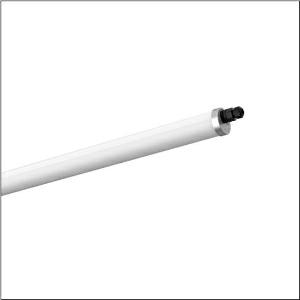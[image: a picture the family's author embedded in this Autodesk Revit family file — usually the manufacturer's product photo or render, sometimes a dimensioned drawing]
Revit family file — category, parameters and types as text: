
# Revit family: monsun_r__31_tube_51ft107n4a0a_c9dd
name_source: partatom
category: Lighting Fixtures
units: mm (PartAtom-declared; Revit-internal decimal feet)

## family parameters
Cut with Voids When Loaded = No
Host = Face
Light Source = No
Part Type = Normal
Room Calculation Point = No
Round Connector Dimension = Use Diameter
Shared = No

## types (1)
- Monsun® 31 Tube (1 x LED, 10000 lm, 58 W, 4000K)
    Apparent Load = 58 VA
    CIE Flux Codes = 42 71 90 91 100
    Color Rendering = 80
    Color Temperature = 4000K
    Default Elevation = 1800 mm
    Description = Monsun® 31 Tube, tubular luminaire, primary optical cover: diffuser, of PMMA, light emission: direct distribution, primary light characteristic: symmetric, installation type: suspended mounting, surface-mounted, LED, rated luminous flux: 10.000lm, luminous efficacy: 160lm/W, light colour: 840, colour temperature: 4000K, with with 1 terminal, 3-pole, max. 2.5mm², through-wiring: 3x 1.5mm², mains connection: 220..240V, AC, 50/60Hz, rated input power: 58W, housing, cylindrical, of PMMA, semi-transparent, matt white, with luminaire and ceiling fastening, V4A, mounting with brackets of stainless steel, length: 1.560mm, diameter: 75mm, end cap, of stainless steel (V4A), protection rating (complete): IP67/IP69K, insulation class (complete): insulation class I (protective earthing), certification: CE, UKCA, impact resistance: IK07, permissible operating ambient temperature: -20..+40°C, corresponds to IFS (International Featured Standards) requirements for safety and quality in the food industry, usage in unprotected outdoor area possible with horizontal mounting, contact your sales advisor before using the luminaires in applications with unclear chemical exposure, large temperature fluctuations or condensation-forming humidity, packaging unit: 1 piece
    Height = 83 mm
    Lamp = 1 x LED
    Lamp Light Flux = 10000 lm
    Lamp Power = 58 W
    Lamp count = 1
    Length = 1560 mm
    Luminous efficacy = 172 lm/W
    Manufacturer = Siteco
    ModVariant = No
    Model = 51FT107N4A0A
    Mounting Place = Ceiling
    Mounting Type = Pendant
    Number of Poles = 1
    OnlyDefault = Yes
    Power Factor = 1
    Product Name = Monsun® 31 Tube
    Product group = tubular luminaire
    ProductGroupID = 906
    Protection Class = Protection class I
    RLX_Detail_Level = 1
    RLX_Emergency_Light_Flux = 0 lm
    RLX_Emergency_Type = 0
    RLX_Emergency_Type_DB = No
    RlxData = <blob elided: 25329 chars, md5=eb473180>
    Socket = socket
    Standby Power = 0 W
    System Light Flux = 10000 lm
    System Power = 58 W
    Type Comments = Product without accessories
    Type Image = l_1228461.jpg
    URL = http://relux.com
    VarID = ---
    Voltage = 0 V
    Weight = 0.00 kg
    Width = 75 mm

## geometry (parser evidence)
native form markers: Blend x4, Sweep x14
no freeform markers — native parametric forms only
